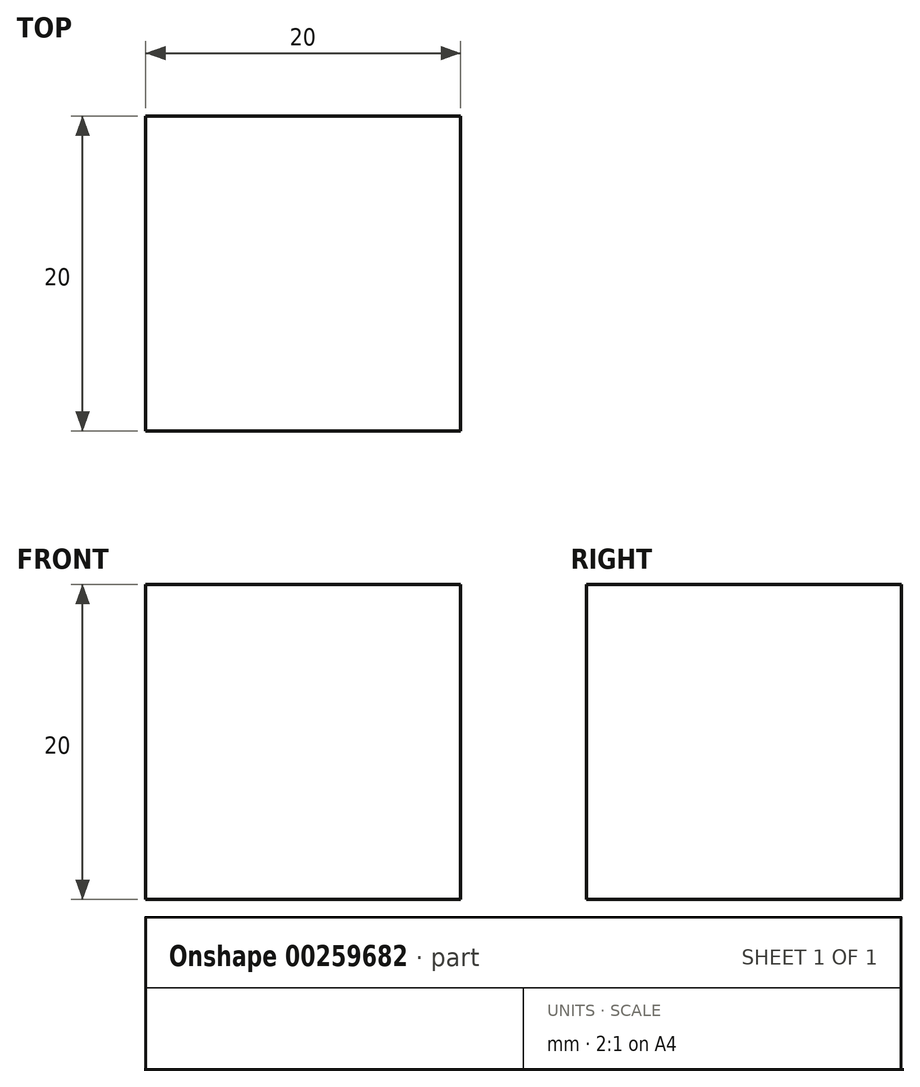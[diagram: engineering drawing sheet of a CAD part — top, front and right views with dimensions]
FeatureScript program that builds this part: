
annotation { "Feature Type Name" : "Feature", "Feature Type Description" : "" }
export const myFeature = defineFeature(function(context is Context, id is Id, definition is map)
    precondition{}
    {
        {
            var Q0;
            Q0=qCreatedBy(makeId("Top.planeOp"),FACE);
            var sketch = newSketch(context, id + "F0", { "sketchPlane" : qUnion([Q0])});
            skLineSegment(sketch, "E0.bottom", {"start": v(10, -10) * mm, "end": v(-10, -10) * mm});
            skLineSegment(sketch, "E0.top", {"start": v(10, 10) * mm, "end": v(-10, 10) * mm});
            skLineSegment(sketch, "E0.left", {"start": v(10, -10) * mm, "end": v(10, 10) * mm});
            skLineSegment(sketch, "E0.right", {"start": v(-10, -10) * mm, "end": v(-10, 10) * mm});
            skPoint(sketch, "E0.middle", {"position": v(0, 0) * mm});
            skSolve(sketch);
        }
        {
            var Q0;
            Q0 = qSketchRegion(id + "F0", true);
            extrude(context, id + "F1", {"entities" : qUnion([Q0]), "depth" : 20 * mm, "offsetDistance" : 25 * mm});
        }
    });
